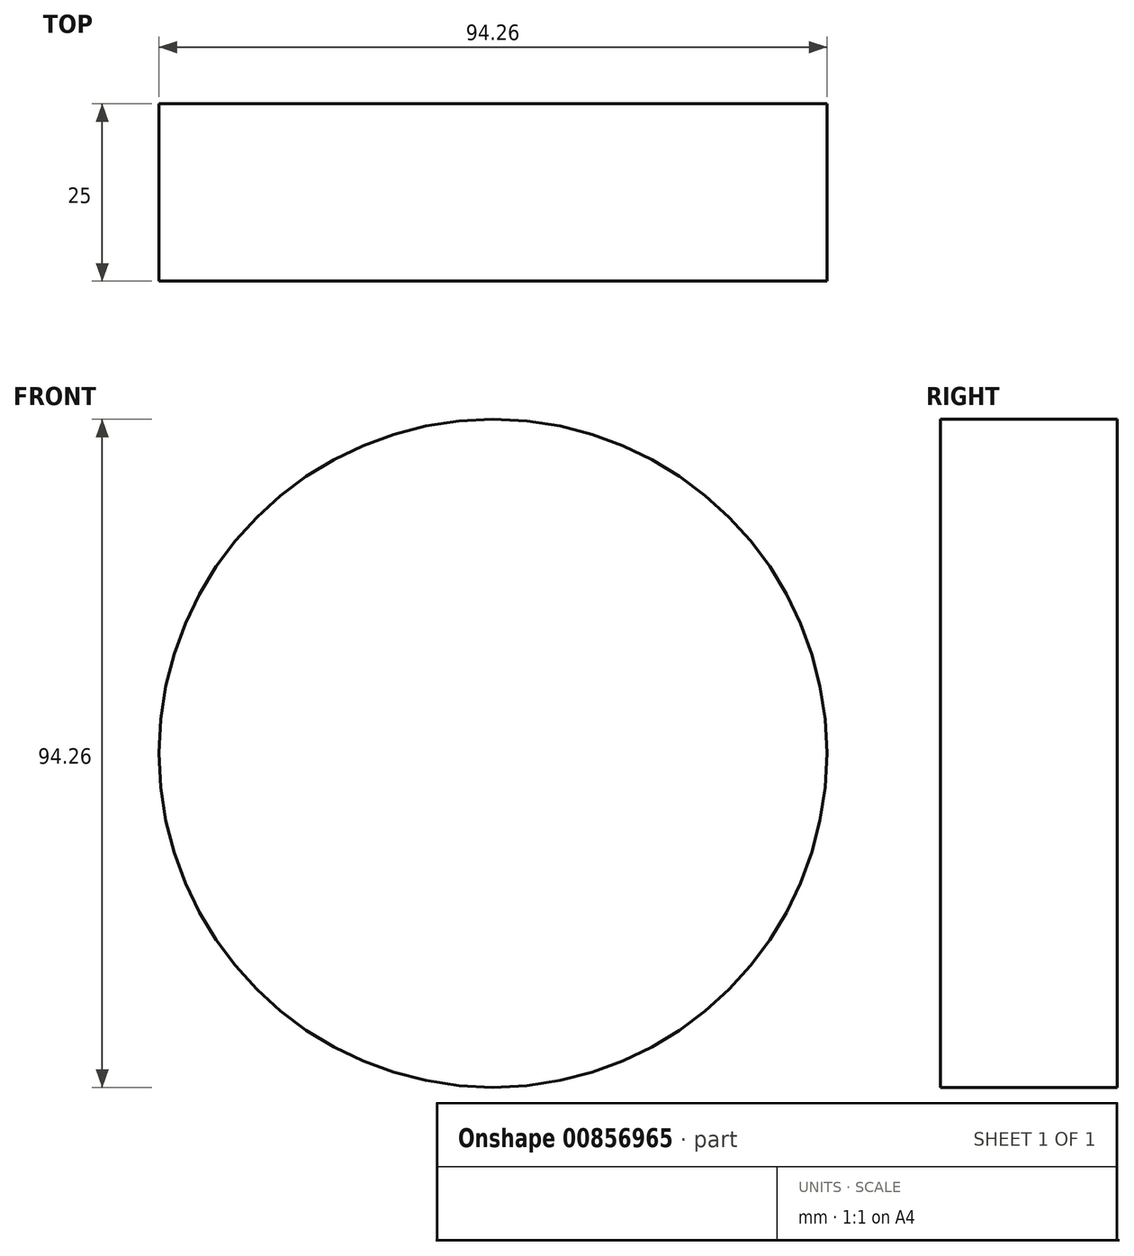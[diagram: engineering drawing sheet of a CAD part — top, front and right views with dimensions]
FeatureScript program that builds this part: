
annotation { "Feature Type Name" : "Feature", "Feature Type Description" : "" }
export const myFeature = defineFeature(function(context is Context, id is Id, definition is map)
    precondition{}
    {
        {
            var Q0;
            Q0=qCreatedBy(makeId("Front.planeOp"),FACE);
            var sketch = newSketch(context, id + "F0", { "sketchPlane" : qUnion([Q0])});
            skCircle(sketch, "E0", {"center": v(0, 0) * mm, "radius": 47.13 * mm});
            skLineSegment(sketch, "E1", {"start": v(0, 0) * mm, "end": v(-31, 35.5) * mm});
            skLineSegment(sketch, "E2", {"start": v(0, 0) * mm, "end": v(32.57, 34.06) * mm});
            skLineSegment(sketch, "E3", {"start": v(0, 0) * mm, "end": v(34.06, -32.57) * mm});
            skLineSegment(sketch, "E4", {"start": v(0, 0) * mm, "end": v(-35.5, -31) * mm});
            skSolve(sketch);
        }
        {
            var Q0;
            Q0 = qSketchRegion(id + "F0", true);
            extrude(context, id + "F1", {"entities" : qUnion([Q0]), "depth" : 25 * mm, "offsetDistance" : 25 * mm});
        }
    });
